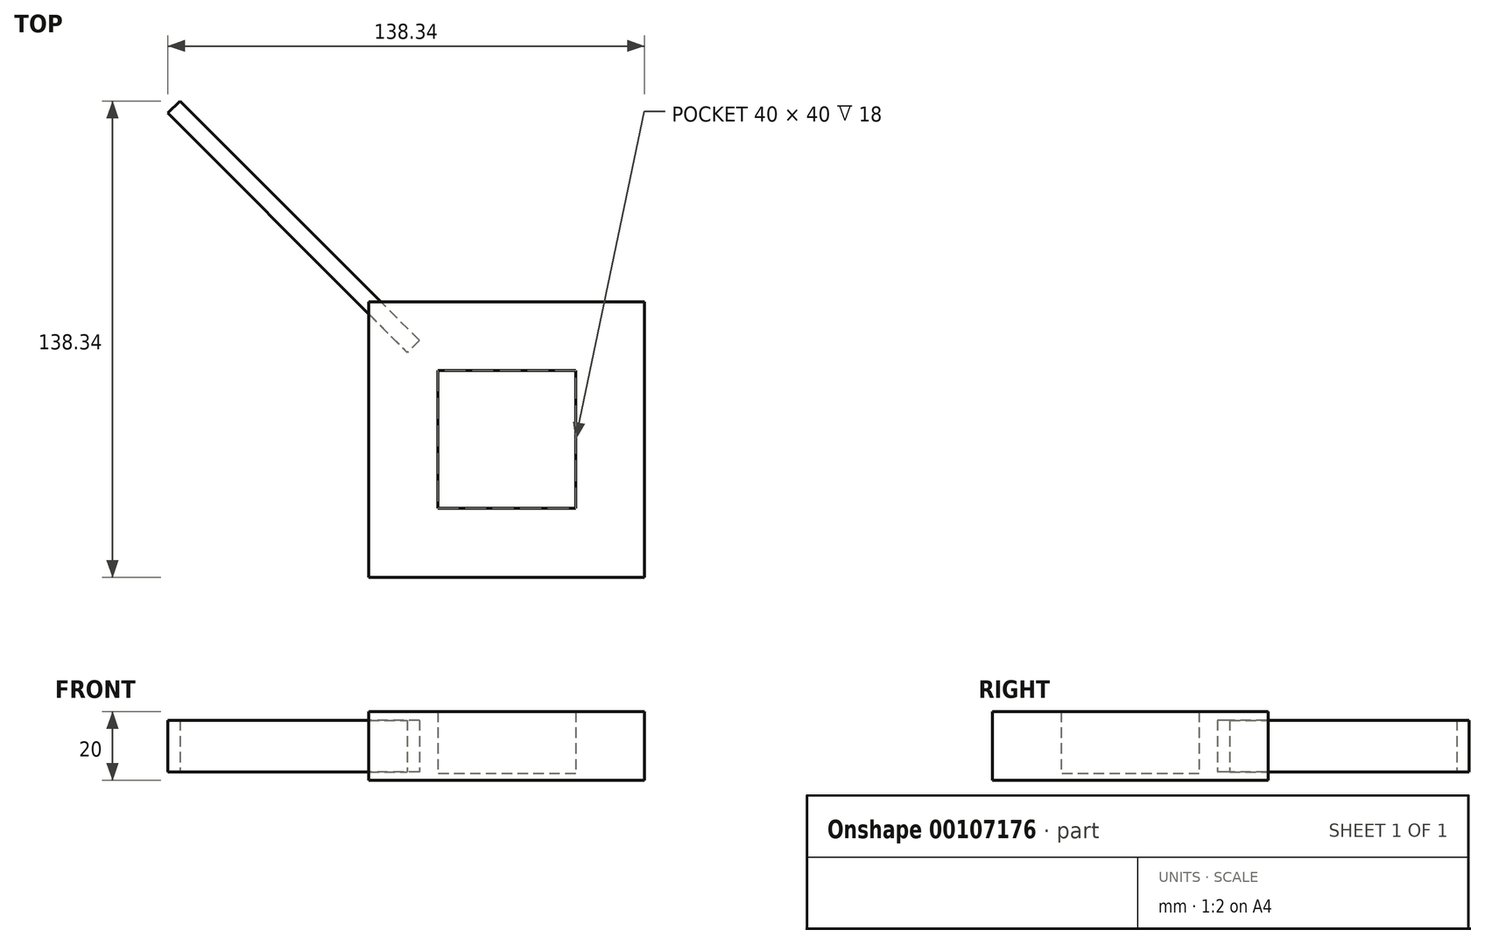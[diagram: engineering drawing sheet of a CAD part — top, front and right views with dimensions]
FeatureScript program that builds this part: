
annotation { "Feature Type Name" : "Feature", "Feature Type Description" : "" }
export const myFeature = defineFeature(function(context is Context, id is Id, definition is map)
    precondition{}
    {
        {
            var Q0;
            Q0=qCreatedBy(makeId("Top.planeOp"),FACE);
            var sketch = newSketch(context, id + "F0", { "sketchPlane" : qUnion([Q0])});
            skLineSegment(sketch, "E0.bottom", {"start": v(40, 40) * mm, "end": v(-40, 40) * mm});
            skLineSegment(sketch, "E0.top", {"start": v(40, -40) * mm, "end": v(-40, -40) * mm});
            skLineSegment(sketch, "E0.left", {"start": v(40, 40) * mm, "end": v(40, -40) * mm});
            skLineSegment(sketch, "E0.right", {"start": v(-40, 40) * mm, "end": v(-40, -40) * mm});
            skPoint(sketch, "E0.middle", {"position": v(0, 0) * mm});
            skLineSegment(sketch, "E1.bottom", {"start": v(20, 20) * mm, "end": v(-20, 20) * mm});
            skLineSegment(sketch, "E1.top", {"start": v(20, -20) * mm, "end": v(-20, -20) * mm});
            skLineSegment(sketch, "E1.left", {"start": v(20, 20) * mm, "end": v(20, -20) * mm});
            skLineSegment(sketch, "E1.right", {"start": v(-20, 20) * mm, "end": v(-20, -20) * mm});
            skLineSegment(sketch, "E2", {"start": v(-20, 0) * mm, "end": v(-40, 0) * mm, "construction": true});
            skSolve(sketch);
        }
        {
            var Q0;
            Q0=makeQuery(id+"F0.imprint","IMPRINT",FACE,{"disambiguationData":[TD([[makeQuery(id+"F0.imprint","IMPRINT",EDGE,{"derivedFrom":sQuery(id+"F0.wireOp",EDGE,"E0.bottom")}),1.0]])]});
            extrude(context, id + "F1", {"entities" : qUnion([Q0]), "depth" : 20 * mm});
        }
        {
            var Q0;
            Q0=makeQuery(id+"F0.imprint","IMPRINT",FACE,{"disambiguationData":[TD([[makeQuery(id+"F0.imprint","IMPRINT",EDGE,{"derivedFrom":sQuery(id+"F0.wireOp",EDGE,"E1.bottom")}),1.0]])]});
            extrude(context, id + "F2", {"entities" : qUnion([Q0]), "operationType" : NewBodyOperationType.ADD, "depth" : 2 * mm});
        }
        {
            var Q0;
            Q0=makeQuery(id+"F1.opExtrude","CAP_FACE",FACE,{"disambiguationData":[OSD([sQuery(id+"F0.wireOp",EDGE,"E0.bottom"),sQuery(id+"F0.wireOp",EDGE,"E0.top"),sQuery(id+"F0.wireOp",EDGE,"E0.left"),sQuery(id+"F0.wireOp",EDGE,"E0.right"),sQuery(id+"F0.wireOp",EDGE,"E1.bottom"),sQuery(id+"F0.wireOp",EDGE,"E1.top"),sQuery(id+"F0.wireOp",EDGE,"E1.left"),sQuery(id+"F0.wireOp",EDGE,"E1.right")])],"isStart":false});
            var Q1;
            {var subQ0=sQuery(id+"F0.wireOp",EDGE,"E1.right");var subQ1=sQuery(id+"F0.wireOp",EDGE,"E1.left");var subQ2=sQuery(id+"F0.wireOp",EDGE,"E1.top");var subQ3=sQuery(id+"F0.wireOp",EDGE,"E1.bottom");Q1=makeQuery(id+"F2.boolean.opBoolean","MERGE",FACE,{"derivedFrom":[makeQuery(id+"F1.opExtrude","CAP_FACE",FACE,{"disambiguationData":[OSD([sQuery(id+"F0.wireOp",EDGE,"E0.bottom"),sQuery(id+"F0.wireOp",EDGE,"E0.top"),sQuery(id+"F0.wireOp",EDGE,"E0.left"),sQuery(id+"F0.wireOp",EDGE,"E0.right"),subQ3,subQ2,subQ1,subQ0])],"isStart":true}),makeQuery(id+"F2.opExtrude","CAP_FACE",FACE,{"disambiguationData":[OSD([subQ3,subQ2,subQ1,subQ0])],"isStart":true})]});}
            cPlane(context, id + "F3", {"entities" : qUnion([Q0, Q1]), "cplaneType" : CPlaneType.MID_PLANE, "offset" : 25 * mm, "width" : 150 * mm, "height" : 150 * mm});
        }
        {
            var Q0;
            Q0=qCreatedBy(id+"F3.planeOp",FACE);
            var sketch = newSketch(context, id + "F4", { "sketchPlane" : qUnion([Q0])});
            skLineSegment(sketch, "E3", {"start": v(0, 0) * mm, "end": v(-96.57, 96.57) * mm, "construction": true});
            skPoint(sketch, "E4.0", {"position": v(-40, 40) * mm});
            skLineSegment(sketch, "E5", {"start": v(0, 0) * mm, "end": v(1.77, 1.77) * mm});
            skLineSegment(sketch, "E6", {"start": v(1.77, 1.77) * mm, "end": v(-94.8, 98.34) * mm});
            skLineSegment(sketch, "E7", {"start": v(-94.8, 98.34) * mm, "end": v(-98.34, 94.8) * mm});
            skLineSegment(sketch, "E8", {"start": v(-98.34, 94.8) * mm, "end": v(-1.77, -1.77) * mm});
            skLineSegment(sketch, "E9", {"start": v(-1.77, -1.77) * mm, "end": v(0, 0) * mm});
            skLineSegment(sketch, "E10", {"start": v(-25.3, 28.84) * mm, "end": v(-28.84, 25.3) * mm});
            skSolve(sketch);
        }
        {
            var Q0;
            {var subQ0=sQuery(id+"F4.wireOp",EDGE,"E7");Q0=makeQuery(id+"F4.imprint","IMPRINT",FACE,{"disambiguationData":[TD([[makeQuery(id+"F4.imprint","IMPRINT",EDGE,{"derivedFrom":subQ0}),1.0]])]});}
            extrude(context, id + "F5", {"entities" : qUnion([Q0]), "endBound" : BoundingType.SYMMETRIC, "depth" : 15 * mm});
        }
    });
